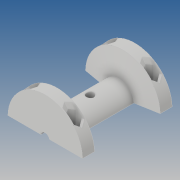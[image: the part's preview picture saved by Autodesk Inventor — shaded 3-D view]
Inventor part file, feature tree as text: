
AUTODESK INVENTOR PART (.ipt)
format: ipt  version: 2019 (Build 230136000, 136)  size: 286,208 bytes
history: native  units: mm
features: other x4, projected_geometry x2, extrude x1, chamfer x1, sketch x1
ambient origin geometry x8: Origin, YZ Plane, XZ Plane, XY Plane, X Axis, Y Axis, Z Axis, Center Point
bodies: Solide1 (feature_tree)
feature tree (9):
  other  "demi_tambour.ipt"
  other  "Plan de construction1"
  extrude  "Extrusion1"  Depth=10.0mm
  chamfer  "Chanfrein1"  Distance=6.9mm
  other  "Solide1::demi_tambour.ipt"
  other  "FonctionRepérage1"
  sketch  "Esquisse1"
  projected_geometry  "Boucle projetée1"
  projected_geometry  "Boucle projetée2"
